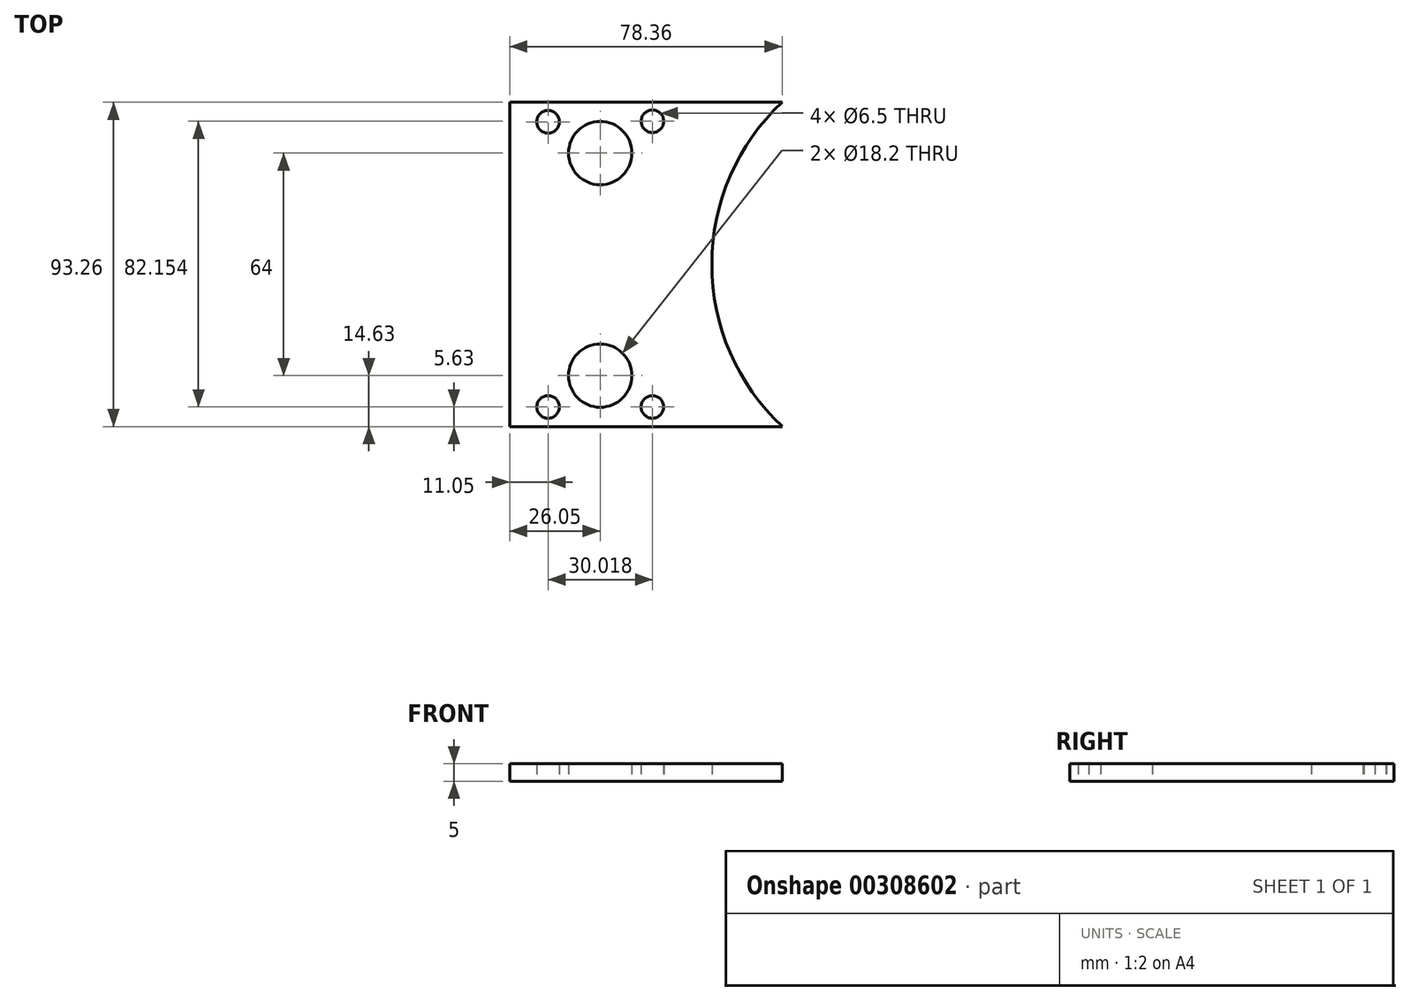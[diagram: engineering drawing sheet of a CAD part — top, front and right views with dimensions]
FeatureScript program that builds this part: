
annotation { "Feature Type Name" : "Feature", "Feature Type Description" : "" }
export const myFeature = defineFeature(function(context is Context, id is Id, definition is map)
    precondition{}
    {
        {
            var Q0;
            Q0=qCreatedBy(makeId("Top.planeOp"),FACE);
            var sketch = newSketch(context, id + "F0", { "sketchPlane" : qUnion([Q0])});
            skCircle(sketch, "E0", {"center": v(0, 0) * mm, "radius": 70.5 * mm});
            skCircle(sketch, "E1", {"center": v(0, 0) * mm, "radius": 60.75 * mm});
            skLineSegment(sketch, "E2", {"start": v(0, 0) * mm, "end": v(-222, 0) * mm, "construction": true});
            skPoint(sketch, "E3", {"position": v(-77, 0) * mm});
            skCircle(sketch, "E4", {"center": v(0, 0) * mm, "radius": 63.9 * mm});
            skPoint(sketch, "E5", {"position": v(-66.29, 24) * mm});
            skPoint(sketch, "E6", {"position": v(-55.8, 24) * mm});
            skPoint(sketch, "E7", {"position": v(-96, 0) * mm});
            skLineSegment(sketch, "E8.bottom", {"start": v(-115, 45.5) * mm, "end": v(-77, 45.5) * mm, "construction": true});
            skLineSegment(sketch, "E8.top", {"start": v(-115, -45.5) * mm, "end": v(-77, -45.5) * mm, "construction": true});
            skLineSegment(sketch, "E8.left", {"start": v(-115, 45.5) * mm, "end": v(-115, -45.5) * mm, "construction": true});
            skLineSegment(sketch, "E8.right", {"start": v(-77, 45.5) * mm, "end": v(-77, -45.5) * mm, "construction": true});
            skLineSegment(sketch, "E9.bottom", {"start": v(-83, 39) * mm, "end": v(-109, 39) * mm, "construction": true});
            skLineSegment(sketch, "E9.top", {"start": v(-83, -39) * mm, "end": v(-109, -39) * mm});
            skLineSegment(sketch, "E9.left", {"start": v(-83, 44) * mm, "end": v(-83, -44) * mm, "construction": true});
            skLineSegment(sketch, "E9.right", {"start": v(-109, 44) * mm, "end": v(-109, -44) * mm, "construction": true});
            skCircle(sketch, "E10", {"center": v(-109, 39) * mm, "radius": 2.5 * mm});
            skCircle(sketch, "E11", {"center": v(-83, 39) * mm, "radius": 2.5 * mm});
            skCircle(sketch, "E12", {"center": v(-109, -39) * mm, "radius": 2.5 * mm});
            skCircle(sketch, "E13", {"center": v(-83, -39) * mm, "radius": 2.5 * mm});
            skLineSegment(sketch, "E14.bottom", {"start": v(-77, 60) * mm, "end": v(-115, 60) * mm});
            skLineSegment(sketch, "E14.top", {"start": v(-77, -60) * mm, "end": v(-115, -60) * mm});
            skLineSegment(sketch, "E14.left", {"start": v(-77, 60) * mm, "end": v(-77, -60) * mm});
            skLineSegment(sketch, "E14.right", {"start": v(-115, 60) * mm, "end": v(-115, -60) * mm});
            skArc(sketch, "E15", {"start": v(-109, 44) * mm, "mid": v(-114, 39) * mm, "end": v(-109, 34) * mm});
            skArc(sketch, "E16", {"start": v(-83, 34) * mm, "mid": v(-78, 39) * mm, "end": v(-83, 44) * mm});
            skLineSegment(sketch, "E17", {"start": v(-109, 44) * mm, "end": v(-83, 44) * mm});
            skLineSegment(sketch, "E18", {"start": v(-109, 34) * mm, "end": v(-83, 34) * mm});
            skArc(sketch, "E19", {"start": v(-109, -34) * mm, "mid": v(-114, -39) * mm, "end": v(-109, -44) * mm});
            skArc(sketch, "E20", {"start": v(-83, -44) * mm, "mid": v(-78, -39) * mm, "end": v(-83, -34) * mm});
            skLineSegment(sketch, "E21", {"start": v(-109, -34) * mm, "end": v(-83, -34) * mm});
            skLineSegment(sketch, "E22", {"start": v(-109, -44) * mm, "end": v(-83, -44) * mm});
            skLineSegment(sketch, "E23", {"start": v(-115, 23) * mm, "end": v(-100, 23) * mm});
            skLineSegment(sketch, "E24", {"start": v(-100, 23) * mm, "end": v(-100, -23) * mm});
            skLineSegment(sketch, "E25", {"start": v(-100, -23) * mm, "end": v(-115, -23) * mm});
            skSolve(sketch);
        }
        {
            var Q0;
            Q0=qCreatedBy(makeId("Top.planeOp"),FACE);
            var sketch = newSketch(context, id + "F1", { "sketchPlane" : qUnion([Q0])});
            skPoint(sketch, "E26.0", {"position": v(-96, 0) * mm});
            skPoint(sketch, "E27.0", {"position": v(0, 0) * mm});
            skCircle(sketch, "E28", {"center": v(0, 0) * mm, "radius": 63.9 * mm});
            skLineSegment(sketch, "E29.bottom", {"start": v(-81, 41) * mm, "end": v(-111, 41) * mm, "construction": true});
            skLineSegment(sketch, "E29.top", {"start": v(-81, -41) * mm, "end": v(-111, -41) * mm, "construction": true});
            skLineSegment(sketch, "E29.left", {"start": v(-81, 41) * mm, "end": v(-81, -41) * mm, "construction": true});
            skLineSegment(sketch, "E29.right", {"start": v(-111, 41) * mm, "end": v(-111, -41) * mm, "construction": true});
            skPoint(sketch, "E30", {"position": v(-111, 41) * mm});
            skPoint(sketch, "E31", {"position": v(-81, 41) * mm});
            skPoint(sketch, "E32", {"position": v(-80.98, 41.15) * mm});
            skPoint(sketch, "E33", {"position": v(-81, -41) * mm});
            skPoint(sketch, "E34", {"position": v(-111, -41) * mm});
            skCircle(sketch, "E35", {"center": v(-111, 41) * mm, "radius": 3.25 * mm});
            skCircle(sketch, "E36", {"center": v(-80.98, 41.15) * mm, "radius": 3.25 * mm});
            skCircle(sketch, "E37", {"center": v(-111, -41) * mm, "radius": 3.25 * mm});
            skCircle(sketch, "E38", {"center": v(-81, -41) * mm, "radius": 3.25 * mm});
            skLineSegment(sketch, "E39.bottom", {"start": v(-37.91, 46.63) * mm, "end": v(-122.05, 46.63) * mm});
            skLineSegment(sketch, "E39.top", {"start": v(-37.91, -46.63) * mm, "end": v(-122.05, -46.63) * mm});
            skLineSegment(sketch, "E39.left", {"start": v(-37.91, 46.63) * mm, "end": v(-37.91, -46.63) * mm});
            skLineSegment(sketch, "E40", {"start": v(-122.05, 46.63) * mm, "end": v(-122.05, -46.63) * mm});
            skLineSegment(sketch, "E41", {"start": v(-96, -46.63) * mm, "end": v(-96, 46.63) * mm, "construction": true});
            skPoint(sketch, "E42", {"position": v(-96, 32) * mm});
            skPoint(sketch, "E43", {"position": v(-96, -32) * mm});
            skCircle(sketch, "E44", {"center": v(-96, 32) * mm, "radius": 9.1 * mm});
            skCircle(sketch, "E45", {"center": v(-96, -32) * mm, "radius": 9.1 * mm});
            skSolve(sketch);
        }
        {
            var Q0;
            Q0=makeQuery(id+"F1.imprint","IMPRINT",FACE,{"disambiguationData":[TD([[makeQuery(id+"F1.imprint","IMPRINT",EDGE,{"derivedFrom":sQuery(id+"F1.wireOp",EDGE,"E35")}),-1.0]])]});
            extrude(context, id + "F2", {"entities" : qUnion([Q0]), "depth" : 5 * mm});
        }
    });
